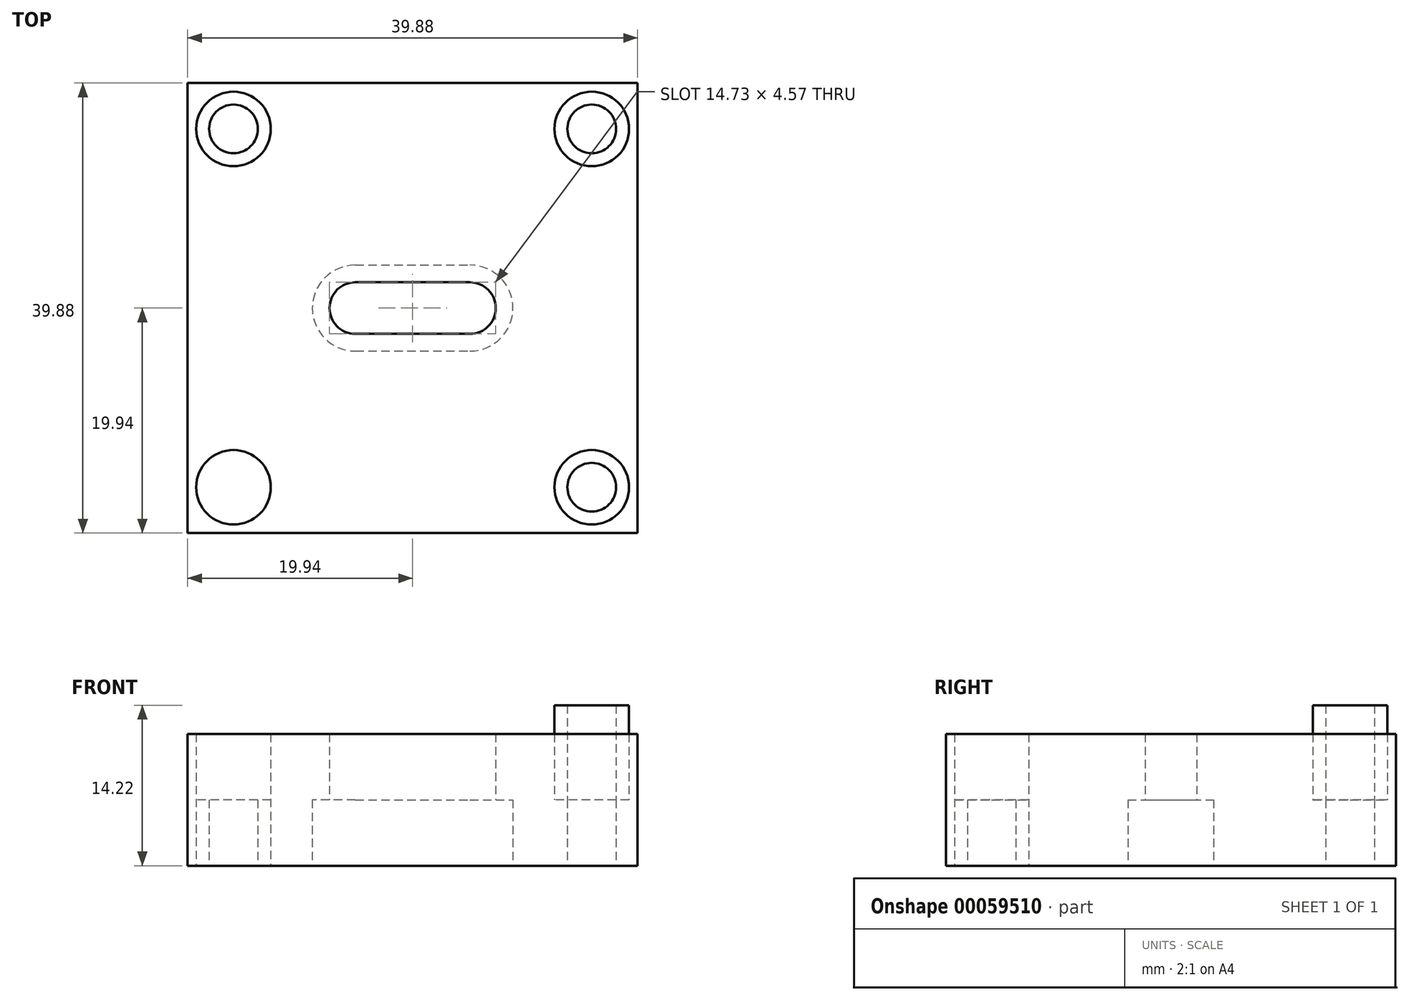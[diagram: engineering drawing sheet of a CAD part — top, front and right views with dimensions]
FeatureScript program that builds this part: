
annotation { "Feature Type Name" : "Feature", "Feature Type Description" : "" }
export const myFeature = defineFeature(function(context is Context, id is Id, definition is map)
    precondition{}
    {
        {
            var Q0;
            Q0=qCreatedBy(makeId("Top.planeOp"),FACE);
            var sketch = newSketch(context, id + "F0", { "sketchPlane" : qUnion([Q0])});
            skLineSegment(sketch, "E0.rect.bottom", {"start": v(19.94, 19.94) * mm, "end": v(-19.94, 19.94) * mm});
            skLineSegment(sketch, "E0.rect.top", {"start": v(19.94, -19.94) * mm, "end": v(-19.94, -19.94) * mm});
            skLineSegment(sketch, "E0.rect.left", {"start": v(19.94, 19.94) * mm, "end": v(19.94, -19.94) * mm});
            skLineSegment(sketch, "E0.rect.right", {"start": v(-19.94, 19.94) * mm, "end": v(-19.94, -19.94) * mm});
            skPoint(sketch, "E0.rect.middle", {"position": v(0, 0) * mm});
            skPoint(sketch, "E1", {"position": v(-15.88, 15.88) * mm});
            skCircle(sketch, "E2", {"center": v(-15.88, 15.88) * mm, "radius": 3.3 * mm});
            skCircle(sketch, "E3", {"center": v(-15.88, 15.88) * mm, "radius": 2.16 * mm});
            skCircle(sketch, "E4.MirrorC", {"center": v(15.88, 15.88) * mm, "radius": 2.16 * mm});
            skCircle(sketch, "E5.MirrorC", {"center": v(15.88, 15.88) * mm, "radius": 3.3 * mm});
            skCircle(sketch, "E6.MirrorC", {"center": v(15.88, -15.88) * mm, "radius": 2.16 * mm});
            skCircle(sketch, "E7.MirrorC", {"center": v(15.88, -15.88) * mm, "radius": 3.3 * mm});
            skCircle(sketch, "E8.MirrorC", {"center": v(-15.88, -15.88) * mm, "radius": 3.3 * mm});
            skCircle(sketch, "E9.MirrorC", {"center": v(-15.88, -15.88) * mm, "radius": 2.16 * mm});
            skLineSegment(sketch, "E10.bottom", {"start": v(19.94, 19.94) * mm, "end": v(7.62, 19.94) * mm});
            skLineSegment(sketch, "E10.top", {"start": v(19.94, -19.94) * mm, "end": v(7.62, -19.94) * mm});
            skLineSegment(sketch, "E10.right", {"start": v(7.62, 19.94) * mm, "end": v(7.62, -19.94) * mm});
            skSolve(sketch);
        }
        {
            var Q0;
            Q0 = qSketchRegion(id + "F0", true);
            var Q1;
            {var subQ1=sQuery(id+"F0.wireOp",EDGE,"a0d088e4-a114-4210-b369-51a1f14ee6a4");var subQ3=makeQuery(id+"F0.imprint","IMPRINT",VERTEX,{"derivedFrom":subQ1});Q1=makeQuery(id+"F0.imprint","IMPRINT",FACE,{"disambiguationData":[TD([[makeQuery(id+"F0.imprint","IMPRINT",EDGE,{"disambiguationData":[TD([[subQ3,1.0]])],"derivedFrom":subQ1}),-1.0]])]});}
            var Q2;
            {var subQ0=sQuery(id+"F0.wireOp",EDGE,"gTe1rfOK-hWQo-2Z0q-ZLt7-7Dn1lkIVvu8e");var subQ1=sQuery(id+"F0.wireOp",EDGE,"5fa916a1-46bb-44d0-9b25-f1613092b9c4");var subQ2=makeQuery(id+"F0.imprint","INTERSECT",VERTEX,{"derivedFrom":[subQ1,subQ0]});Q2=makeQuery(id+"F0.imprint","IMPRINT",FACE,{"disambiguationData":[TD([[makeQuery(id+"F0.imprint","IMPRINT",EDGE,{"disambiguationData":[TD([[subQ2,-1.0]])],"derivedFrom":subQ1}),-1.0]])]});}
            var Q3;
            {var subQ0=sQuery(id+"F0.wireOp",EDGE,"K5YmDXpU-GgtS-j2Cr-nMIa-zNqNAAf7L4pf");var subQ1=sQuery(id+"F0.wireOp",EDGE,"f0f4ba78-e869-495a-b748-71ef774c9df5");var subQ2=makeQuery(id+"F0.imprint","INTERSECT",VERTEX,{"derivedFrom":[subQ1,subQ0]});Q3=makeQuery(id+"F0.imprint","IMPRINT",FACE,{"disambiguationData":[TD([[makeQuery(id+"F0.imprint","IMPRINT",EDGE,{"disambiguationData":[TD([[subQ2,1.0]])],"derivedFrom":subQ1}),1.0]])]});}
            var Q4;
            {var subQ0=sQuery(id+"F0.wireOp",EDGE,"K5YmDXpU-GgtS-j2Cr-nMIa-zNqNAAf7L4pf");var subQ1=sQuery(id+"F0.wireOp",EDGE,"5fa916a1-46bb-44d0-9b25-f1613092b9c4");var subQ2=makeQuery(id+"F0.imprint","INTERSECT",VERTEX,{"derivedFrom":[subQ1,subQ0]});Q4=makeQuery(id+"F0.imprint","IMPRINT",FACE,{"disambiguationData":[TD([[makeQuery(id+"F0.imprint","IMPRINT",EDGE,{"disambiguationData":[TD([[subQ2,-1.0]])],"derivedFrom":subQ1}),-1.0]])]});}
            var Q5;
            {var subQ0=sQuery(id+"F0.wireOp",EDGE,"K5YmDXpU-GgtS-j2Cr-nMIa-zNqNAAf7L4pf");var subQ1=sQuery(id+"F0.wireOp",EDGE,"5fa916a1-46bb-44d0-9b25-f1613092b9c4");var subQ2=makeQuery(id+"F0.imprint","INTERSECT",VERTEX,{"derivedFrom":[subQ1,subQ0]});Q5=makeQuery(id+"F0.imprint","IMPRINT",FACE,{"disambiguationData":[TD([[makeQuery(id+"F0.imprint","IMPRINT",EDGE,{"disambiguationData":[TD([[subQ2,-1.0]])],"derivedFrom":subQ1}),1.0]])]});}
            var Q6;
            {var subQ4=sQuery(id+"F0.wireOp",EDGE,"5fa916a1-46bb-44d0-9b25-f1613092b9c4");var subQ6=makeQuery(id+"F0.imprint","INTERSECT",VERTEX,{"derivedFrom":[subQ4,sQuery(id+"F0.wireOp",EDGE,"gTe1rfOK-hWQo-2Z0q-ZLt7-7Dn1lkIVvu8e")]});Q6=makeQuery(id+"F0.imprint","IMPRINT",FACE,{"disambiguationData":[TD([[makeQuery(id+"F0.imprint","IMPRINT",EDGE,{"disambiguationData":[TD([[subQ6,-1.0]])],"derivedFrom":subQ4}),1.0]])]});}
            var Q7;
            {var subQ0=sQuery(id+"F0.wireOp",EDGE,"rkYheQmR-etU9-h3Yq-UIZ2-16BNES9nIO10");Q7=makeQuery(id+"F0.imprint","IMPRINT",FACE,{"disambiguationData":[TD([[makeQuery(id+"F0.imprint","IMPRINT",EDGE,{"derivedFrom":subQ0}),1.0]])]});}
            extrude(context, id + "F1", {"entities" : qUnion([Q0, Q1, Q2, Q3, Q4, Q5, Q6, Q7]), "depth" : 11.68 * mm});
        }
        {
            var Q0;
            Q0=makeQuery(id+"F0.imprint","IMPRINT",FACE,{"disambiguationData":[TD([[makeQuery(id+"F0.imprint","IMPRINT",EDGE,{"derivedFrom":sQuery(id+"F0.wireOp",EDGE,"E2")}),1.0]])]});
            var Q1;
            Q1=makeQuery(id+"F0.imprint","IMPRINT",FACE,{"disambiguationData":[TD([[makeQuery(id+"F0.imprint","IMPRINT",EDGE,{"derivedFrom":sQuery(id+"F0.wireOp",EDGE,"E4.MirrorC")}),1.0]])]});
            var Q2;
            Q2=makeQuery(id+"F0.imprint","IMPRINT",FACE,{"disambiguationData":[TD([[makeQuery(id+"F0.imprint","IMPRINT",EDGE,{"derivedFrom":sQuery(id+"F0.wireOp",EDGE,"E6.MirrorC")}),-1.0]])]});
            var Q3;
            Q3=makeQuery(id+"F0.imprint","IMPRINT",FACE,{"disambiguationData":[TD([[makeQuery(id+"F0.imprint","IMPRINT",EDGE,{"derivedFrom":sQuery(id+"F0.wireOp",EDGE,"E8.MirrorC")}),-1.0]])]});
            extrude(context, id + "F2", {"entities" : qUnion([Q0, Q1, Q2, Q3]), "operationType" : NewBodyOperationType.ADD, "depth" : 5.84 * mm});
        }
        {
            var Q0;
            Q0=makeQuery(id+"F0.imprint","IMPRINT",FACE,{"disambiguationData":[TD([[makeQuery(id+"F0.imprint","IMPRINT",EDGE,{"derivedFrom":sQuery(id+"F0.wireOp",EDGE,"E5.MirrorC")}),1.0]])]});
            extrude(context, id + "F3", {"entities" : qUnion([Q0]), "operationType" : NewBodyOperationType.ADD, "depth" : 14.22 * mm});
        }
        {
            var Q0;
            {var subQ0=sQuery(id+"F0.wireOp",EDGE,"E8.MirrorC");var subQ1=sQuery(id+"F0.wireOp",EDGE,"E7.MirrorC");var subQ2=sQuery(id+"F0.wireOp",EDGE,"E5.MirrorC");var subQ3=sQuery(id+"F0.wireOp",EDGE,"E2");Q0=makeQuery(id+"F2.boolean.opBoolean","MERGE",FACE,{"derivedFrom":[makeQuery(id+"F1.opExtrude","CAP_FACE",FACE,{"disambiguationData":[OSD([sQuery(id+"F0.wireOp",EDGE,"E0.rect.bottom"),sQuery(id+"F0.wireOp",EDGE,"E0.rect.top"),sQuery(id+"F0.wireOp",EDGE,"E0.rect.right"),subQ3,subQ2,subQ1,subQ0,sQuery(id+"F0.wireOp",EDGE,"E10.bottom"),sQuery(id+"F0.wireOp",EDGE,"E10.top"),sQuery(id+"F0.wireOp",EDGE,"E0.rect.left")])],"isStart":true}),makeQuery(id+"F2.opExtrude","CAP_FACE",FACE,{"disambiguationData":[OSD([subQ3,sQuery(id+"F0.wireOp",EDGE,"E3")])],"isStart":true}),makeQuery(id+"F2.opExtrude","CAP_FACE",FACE,{"disambiguationData":[OSD([sQuery(id+"F0.wireOp",EDGE,"E4.MirrorC"),subQ2])],"isStart":true}),makeQuery(id+"F2.opExtrude","CAP_FACE",FACE,{"disambiguationData":[OSD([sQuery(id+"F0.wireOp",EDGE,"E6.MirrorC"),subQ1])],"isStart":true}),makeQuery(id+"F2.opExtrude","CAP_FACE",FACE,{"disambiguationData":[OSD([subQ0,sQuery(id+"F0.wireOp",EDGE,"E9.MirrorC")])],"isStart":true})]});}
            var sketch = newSketch(context, id + "F4", { "sketchPlane" : qUnion([Q0])});
            skCircle(sketch, "E11", {"center": v(5.08, 0) * mm, "radius": 3.81 * mm});
            skCircle(sketch, "E12", {"center": v(5.08, 0) * mm, "radius": 2.29 * mm});
            skLineSegment(sketch, "E13", {"start": v(7.62, 19.94) * mm, "end": v(7.62, -19.94) * mm, "construction": true});
            skCircle(sketch, "E14", {"center": v(-5.08, 0) * mm, "radius": 2.29 * mm});
            skCircle(sketch, "E15", {"center": v(-5.08, 0) * mm, "radius": 3.81 * mm});
            skLineSegment(sketch, "E16", {"start": v(-5.08, 2.29) * mm, "end": v(5.08, 2.29) * mm});
            skLineSegment(sketch, "E17", {"start": v(5.08, -2.29) * mm, "end": v(-5.08, -2.29) * mm});
            skLineSegment(sketch, "E18", {"start": v(-5.08, -3.81) * mm, "end": v(5.08, -3.81) * mm});
            skLineSegment(sketch, "E19", {"start": v(-5.08, 3.8) * mm, "end": v(5.08, 3.8) * mm});
            skSolve(sketch);
        }
        {
            var Q0;
            {var subQ0=sQuery(id+"F4.wireOp",EDGE,"E14");var subQ1=makeQuery(id+"F4.imprint","INTERSECT",VERTEX,{"derivedFrom":[subQ0,sQuery(id+"F4.wireOp",EDGE,"E16")]});Q0=makeQuery(id+"F4.imprint","IMPRINT",FACE,{"disambiguationData":[TD([[makeQuery(id+"F4.imprint","IMPRINT",EDGE,{"disambiguationData":[TD([[subQ1,-1.0]])],"derivedFrom":subQ0}),1.0]])]});}
            var Q1;
            {var subQ0=sQuery(id+"F4.wireOp",EDGE,"E12");var subQ1=makeQuery(id+"F4.imprint","INTERSECT",VERTEX,{"derivedFrom":[subQ0,sQuery(id+"F4.wireOp",EDGE,"E16")]});Q1=makeQuery(id+"F4.imprint","IMPRINT",FACE,{"disambiguationData":[TD([[makeQuery(id+"F4.imprint","IMPRINT",EDGE,{"disambiguationData":[TD([[subQ1,-1.0]])],"derivedFrom":subQ0}),1.0]])]});}
            var Q2;
            {var subQ0=sQuery(id+"F4.wireOp",EDGE,"E16");var subQ1=sQuery(id+"F4.wireOp",EDGE,"E14");var subQ2=makeQuery(id+"F4.imprint","INTERSECT",VERTEX,{"derivedFrom":[subQ1,subQ0]});Q2=makeQuery(id+"F4.imprint","IMPRINT",FACE,{"disambiguationData":[TD([[makeQuery(id+"F4.imprint","IMPRINT",EDGE,{"disambiguationData":[TD([[subQ2,1.0]])],"derivedFrom":subQ1}),-1.0]])]});}
            var Q3;
            {var subQ0=sQuery(id+"F4.wireOp",EDGE,"E16");var subQ1=sQuery(id+"F4.wireOp",EDGE,"E11");var subQ2=makeQuery(id+"F4.imprint","INTERSECT",VERTEX,{"derivedFrom":[subQ1,subQ0]});Q3=makeQuery(id+"F4.imprint","IMPRINT",FACE,{"disambiguationData":[TD([[makeQuery(id+"F4.imprint","IMPRINT",EDGE,{"disambiguationData":[TD([[subQ2,-1.0]])],"derivedFrom":subQ1}),-1.0]])]});}
            var Q4;
            {var subQ0=sQuery(id+"F4.wireOp",EDGE,"E16");var subQ1=sQuery(id+"F4.wireOp",EDGE,"E11");var subQ2=makeQuery(id+"F4.imprint","INTERSECT",VERTEX,{"derivedFrom":[subQ1,subQ0]});Q4=makeQuery(id+"F4.imprint","IMPRINT",FACE,{"disambiguationData":[TD([[makeQuery(id+"F4.imprint","IMPRINT",EDGE,{"disambiguationData":[TD([[subQ2,-1.0]])],"derivedFrom":subQ1}),1.0]])]});}
            extrude(context, id + "F5", {"entities" : qUnion([Q0, Q1, Q2, Q3, Q4]), "operationType" : NewBodyOperationType.REMOVE, "oppositeDirection" : true, "depth" : 25.4 * mm});
        }
        {
            var Q0;
            {var subQ0=sQuery(id+"F4.wireOp",EDGE,"E16");var subQ1=sQuery(id+"F4.wireOp",EDGE,"E14");var subQ2=makeQuery(id+"F4.imprint","INTERSECT",VERTEX,{"derivedFrom":[subQ1,subQ0]});Q0=makeQuery(id+"F4.imprint","IMPRINT",FACE,{"disambiguationData":[TD([[makeQuery(id+"F4.imprint","IMPRINT",EDGE,{"disambiguationData":[TD([[subQ2,1.0]])],"derivedFrom":subQ1}),-1.0]])]});}
            var Q1;
            {var subQ3=sQuery(id+"F4.wireOp",EDGE,"E16");var subQ4=sQuery(id+"F4.wireOp",EDGE,"E14");var subQ5=makeQuery(id+"F4.imprint","INTERSECT",VERTEX,{"derivedFrom":[subQ4,subQ3]});Q1=makeQuery(id+"F4.imprint","IMPRINT",FACE,{"disambiguationData":[TD([[makeQuery(id+"F4.imprint","IMPRINT",EDGE,{"disambiguationData":[TD([[subQ5,-1.0]])],"derivedFrom":subQ4}),-1.0]])]});}
            var Q2;
            {var subQ0=sQuery(id+"F4.wireOp",EDGE,"E19");Q2=makeQuery(id+"F4.imprint","IMPRINT",FACE,{"disambiguationData":[TD([[makeQuery(id+"F4.imprint","IMPRINT",EDGE,{"derivedFrom":subQ0}),-1.0]])]});}
            var Q3;
            {var subQ0=sQuery(id+"F4.wireOp",EDGE,"E16");var subQ1=sQuery(id+"F4.wireOp",EDGE,"E11");var subQ2=makeQuery(id+"F4.imprint","INTERSECT",VERTEX,{"derivedFrom":[subQ1,subQ0]});Q3=makeQuery(id+"F4.imprint","IMPRINT",FACE,{"disambiguationData":[TD([[makeQuery(id+"F4.imprint","IMPRINT",EDGE,{"disambiguationData":[TD([[subQ2,-1.0]])],"derivedFrom":subQ1}),-1.0]])]});}
            var Q4;
            {var subQ0=sQuery(id+"F4.wireOp",EDGE,"E16");var subQ1=sQuery(id+"F4.wireOp",EDGE,"E11");var subQ2=makeQuery(id+"F4.imprint","INTERSECT",VERTEX,{"derivedFrom":[subQ1,subQ0]});Q4=makeQuery(id+"F4.imprint","IMPRINT",FACE,{"disambiguationData":[TD([[makeQuery(id+"F4.imprint","IMPRINT",EDGE,{"disambiguationData":[TD([[subQ2,-1.0]])],"derivedFrom":subQ1}),1.0]])]});}
            var Q5;
            {var subQ5=sQuery(id+"F4.wireOp",EDGE,"E11");var subQ7=makeQuery(id+"F4.imprint","INTERSECT",VERTEX,{"derivedFrom":[subQ5,sQuery(id+"F4.wireOp",EDGE,"E19")]});Q5=makeQuery(id+"F4.imprint","IMPRINT",FACE,{"disambiguationData":[TD([[makeQuery(id+"F4.imprint","IMPRINT",EDGE,{"disambiguationData":[TD([[subQ7,-1.0]])],"derivedFrom":subQ5}),1.0]])]});}
            var Q6;
            {var subQ0=sQuery(id+"F4.wireOp",EDGE,"E18");Q6=makeQuery(id+"F4.imprint","IMPRINT",FACE,{"disambiguationData":[TD([[makeQuery(id+"F4.imprint","IMPRINT",EDGE,{"derivedFrom":subQ0}),1.0]])]});}
            extrude(context, id + "F6", {"entities" : qUnion([Q0, Q1, Q2, Q3, Q4, Q5, Q6]), "operationType" : NewBodyOperationType.REMOVE, "oppositeDirection" : true, "depth" : 5.84 * mm});
        }
    });
